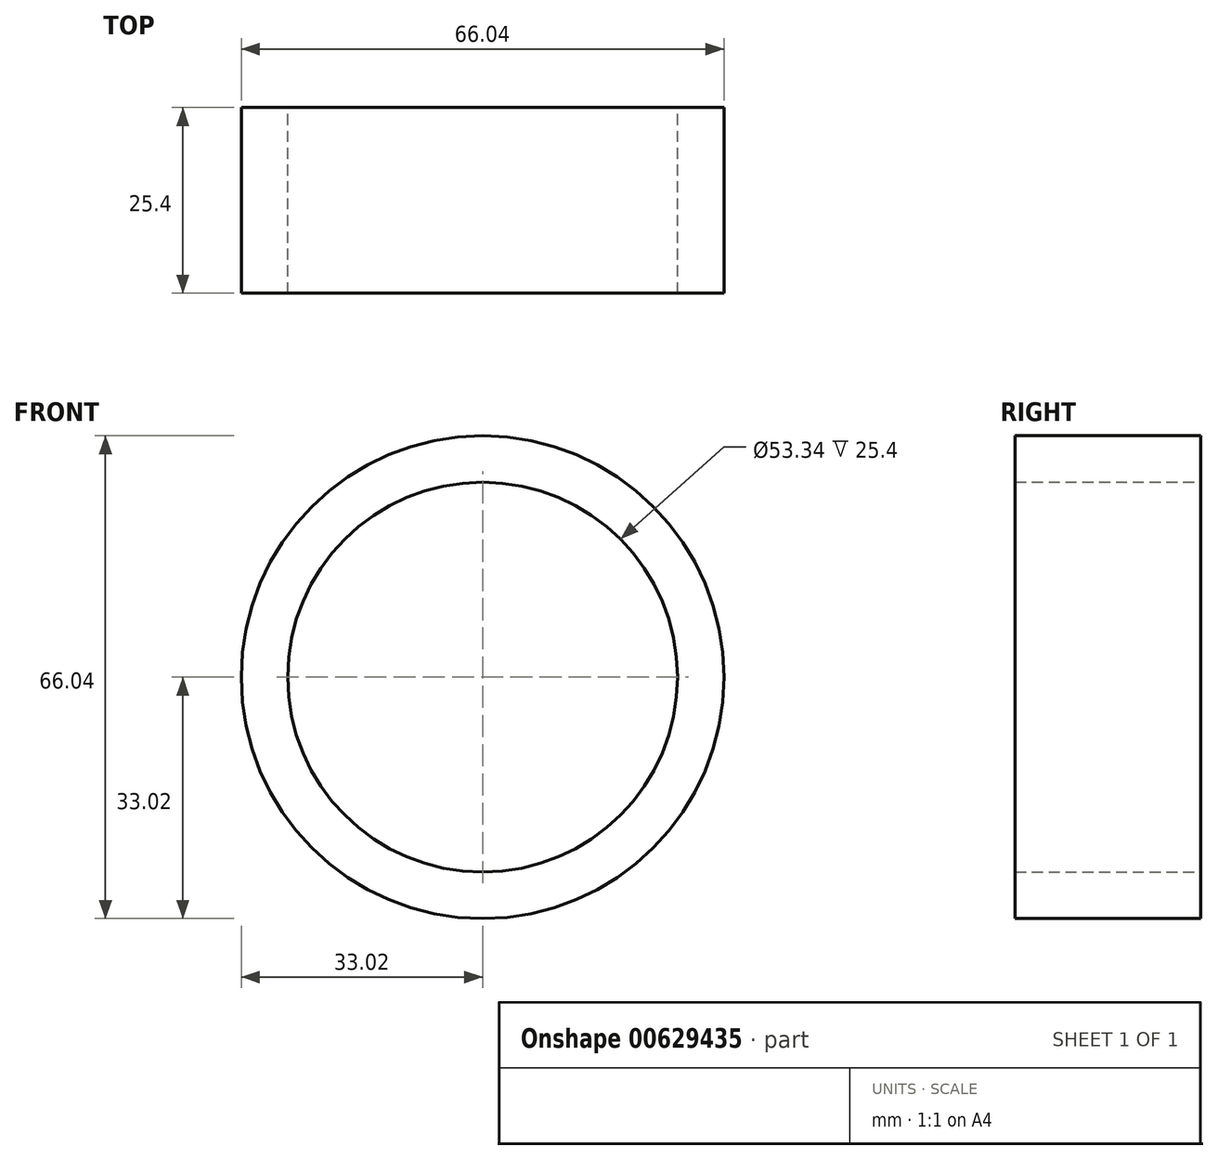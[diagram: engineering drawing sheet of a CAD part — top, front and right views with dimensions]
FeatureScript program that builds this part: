
annotation { "Feature Type Name" : "Feature", "Feature Type Description" : "" }
export const myFeature = defineFeature(function(context is Context, id is Id, definition is map)
    precondition{}
    {
        {
            var Q0;
            Q0=qCreatedBy(makeId("Front.planeOp"),FACE);
            var sketch = newSketch(context, id + "F0", { "sketchPlane" : qUnion([Q0])});
            skCircle(sketch, "E0", {"center": v(0, 0) * mm, "radius": 33.02 * mm});
            skCircle(sketch, "E1.0", {"center": v(0, 0) * mm, "radius": 26.67 * mm});
            skSolve(sketch);
        }
        {
            var Q0;
            Q0 = qSketchRegion(id + "F0", true);
            extrude(context, id + "F1", {"entities" : qUnion([Q0]), "depth" : 25.4 * mm, "offsetDistance" : 25.4 * mm});
        }
    });
